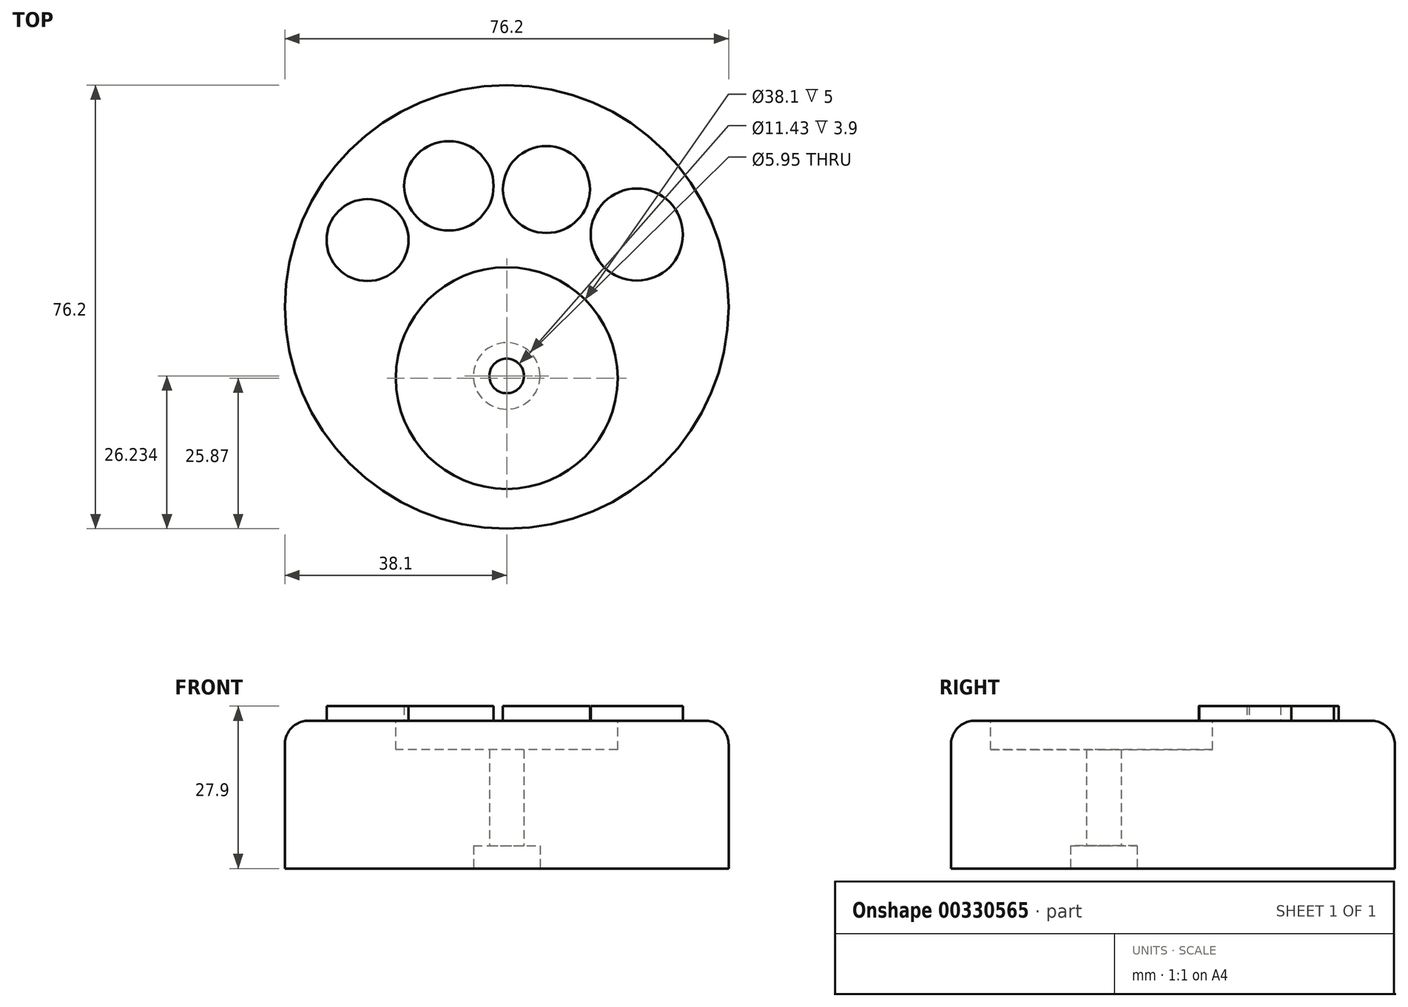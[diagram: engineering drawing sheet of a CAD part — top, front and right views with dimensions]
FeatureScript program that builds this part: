
annotation { "Feature Type Name" : "Feature", "Feature Type Description" : "" }
export const myFeature = defineFeature(function(context is Context, id is Id, definition is map)
    precondition{}
    {
        {
            var Q0;
            Q0=qCreatedBy(makeId("Top.planeOp"),FACE);
            var sketch = newSketch(context, id + "F0", { "sketchPlane" : qUnion([Q0])});
            skCircle(sketch, "E0", {"center": v(0, -4.2) * mm, "radius": 38.1 * mm});
            skSolve(sketch);
        }
        {
            var Q0;
            Q0=qCreatedBy(makeId("Top.planeOp"),FACE);
            var sketch = newSketch(context, id + "F1", { "sketchPlane" : qUnion([Q0])});
            skSolve(sketch);
        }
        {
            var Q0;
            Q0=makeQuery(id+"F1.imprint","IMPRINT",FACE,{"disambiguationData":[TD([[makeQuery(id+"F1.imprint","IMPRINT",EDGE,{"derivedFrom":sQuery(id+"F1.wireOp",EDGE,"EjYEmMLQ-RMnw-RSJ6-Yy3C-PBuiI4cfQdJM.bottom")}),-1.0]])]});
            var Q1;
            Q1=makeQuery(id+"F0.imprint","IMPRINT",FACE,{"disambiguationData":[TD([[makeQuery(id+"F0.imprint","IMPRINT",EDGE,{"derivedFrom":sQuery(id+"F0.wireOp",EDGE,"E0")}),1.0]])]});
            extrude(context, id + "F2", {"entities" : qUnion([Q0, Q1]), "depth" : 25.4 * mm});
        }
        {
            var Q0;
            Q0=makeQuery(id+"F2.opExtrude","CAP_EDGE",EDGE,{"disambiguationData":[OSD([sQuery(id+"F0.wireOp",EDGE,"E0")])],"isStart":false});
            var Q1;
            Q1=makeQuery(id+"F2.opExtrude","CAP_EDGE",EDGE,{"disambiguationData":[OSD([sQuery(id+"F1.wireOp",EDGE,"EjYEmMLQ-RMnw-RSJ6-Yy3C-PBuiI4cfQdJM.left")])],"isStart":false});
            var Q2;
            Q2=makeQuery(id+"F2.opExtrude","CAP_EDGE",EDGE,{"disambiguationData":[OSD([sQuery(id+"F1.wireOp",EDGE,"EjYEmMLQ-RMnw-RSJ6-Yy3C-PBuiI4cfQdJM.top")])],"isStart":false});
            var Q3;
            Q3=makeQuery(id+"F2.opExtrude","CAP_EDGE",EDGE,{"disambiguationData":[OSD([sQuery(id+"F1.wireOp",EDGE,"EjYEmMLQ-RMnw-RSJ6-Yy3C-PBuiI4cfQdJM.right")])],"isStart":false});
            fillet(context, id + "F3", {"entities" : qUnion([Q0, Q1, Q2, Q3]), "radius" : 4.1 * mm, "tangentPropagation" : true, "allowEdgeOverflow" : false});
        }
        {
            var Q0;
            Q0=makeQuery(id+"F2.opExtrude","CAP_FACE",FACE,{"disambiguationData":[OSD([sQuery(id+"F0.wireOp",EDGE,"E0")])],"isStart":false});
            var sketch = newSketch(context, id + "F4", { "sketchPlane" : qUnion([Q0])});
            skCircle(sketch, "E1", {"center": v(0, -17.84) * mm, "radius": 19.05 * mm});
            skCircle(sketch, "E2", {"center": v(22.34, 8.22) * mm, "radius": 7.91 * mm});
            skCircle(sketch, "E3", {"center": v(6.83, 15.98) * mm, "radius": 7.47 * mm});
            skCircle(sketch, "E4", {"center": v(-9.93, 16.6) * mm, "radius": 7.68 * mm});
            skCircle(sketch, "E5", {"center": v(-23.9, 7.3) * mm, "radius": 7.03 * mm});
            skSolve(sketch);
        }
        {
            var Q0;
            Q0=makeQuery(id+"F2.opExtrude","CAP_FACE",FACE,{"disambiguationData":[OSD([sQuery(id+"F0.wireOp",EDGE,"E0")])],"isStart":false});
            var sketch = newSketch(context, id + "F5", { "sketchPlane" : qUnion([Q0])});
            skSolve(sketch);
        }
        {
            var Q0;
            Q0=makeQuery(id+"F4.imprint","IMPRINT",FACE,{"disambiguationData":[TD([[makeQuery(id+"F4.imprint","IMPRINT",EDGE,{"derivedFrom":sQuery(id+"F4.wireOp",EDGE,"E4")}),1.0]])]});
            var Q1;
            Q1=makeQuery(id+"F4.imprint","IMPRINT",FACE,{"disambiguationData":[TD([[makeQuery(id+"F4.imprint","IMPRINT",EDGE,{"derivedFrom":sQuery(id+"F4.wireOp",EDGE,"E3")}),1.0]])]});
            var Q2;
            Q2=makeQuery(id+"F4.imprint","IMPRINT",FACE,{"disambiguationData":[TD([[makeQuery(id+"F4.imprint","IMPRINT",EDGE,{"derivedFrom":sQuery(id+"F4.wireOp",EDGE,"E2")}),1.0]])]});
            var Q3;
            Q3=makeQuery(id+"F4.imprint","IMPRINT",FACE,{"disambiguationData":[TD([[makeQuery(id+"F4.imprint","IMPRINT",EDGE,{"derivedFrom":sQuery(id+"F4.wireOp",EDGE,"E5")}),1.0]])]});
            extrude(context, id + "F6", {"entities" : qUnion([Q0, Q1, Q2, Q3]), "operationType" : NewBodyOperationType.ADD, "depth" : 2.5 * mm});
        }
        {
            var Q0;
            {var subQ0=sQuery(id+"F0.wireOp",EDGE,"E0");Q0=makeQuery(id+"F5.imprint","IMPRINT",FACE,{"disambiguationData":[TD([[makeQuery(id+"F5.imprint","IMPRINT",EDGE,{"derivedFrom":makeQuery(id+"F3.opFillet","BLEND_EDGE",EDGE,{"blendedFrom":[makeQuery(id+"F2.opExtrude","CAP_EDGE",EDGE,{"disambiguationData":[OSD([subQ0])],"isStart":false}),makeQuery(id+"F2.opExtrude","CAP_FACE",FACE,{"disambiguationData":[OSD([subQ0])],"isStart":false})],"blendedInto":[makeQuery(id+"F2.opExtrude","CAP_FACE",FACE,{"disambiguationData":[OSD([subQ0])],"isStart":false})]})}),1.0]])]});}
            var sketch = newSketch(context, id + "F7", { "sketchPlane" : qUnion([Q0])});
            skCircle(sketch, "E6", {"center": v(0, -16.42) * mm, "radius": 19.05 * mm});
            skSolve(sketch);
        }
        {
            var Q0;
            Q0=makeQuery(id+"F7.imprint","IMPRINT",FACE,{"disambiguationData":[TD([[makeQuery(id+"F7.imprint","IMPRINT",EDGE,{"derivedFrom":sQuery(id+"F7.wireOp",EDGE,"E6")}),1.0]])]});
            extrude(context, id + "F8", {"entities" : qUnion([Q0]), "operationType" : NewBodyOperationType.REMOVE, "oppositeDirection" : true, "depth" : 5 * mm});
        }
        {
            var Q0;
            Q0=makeQuery(id+"F2.opExtrude","CAP_FACE",FACE,{"disambiguationData":[OSD([sQuery(id+"F0.wireOp",EDGE,"E0")])],"isStart":true});
            var sketch = newSketch(context, id + "F9", { "sketchPlane" : qUnion([Q0])});
            skCircle(sketch, "E7", {"center": v(0, 16.06) * mm, "radius": 5.72 * mm});
            skSolve(sketch);
        }
        {
            var Q0;
            Q0=makeQuery(id+"F9.imprint","IMPRINT",FACE,{"disambiguationData":[TD([[makeQuery(id+"F9.imprint","IMPRINT",EDGE,{"derivedFrom":sQuery(id+"F9.wireOp",EDGE,"E7")}),1.0]])]});
            extrude(context, id + "F10", {"entities" : qUnion([Q0]), "operationType" : NewBodyOperationType.REMOVE, "oppositeDirection" : true, "depth" : 3.9 * mm});
        }
        {
            var Q0;
            Q0=makeQuery(id+"F10.boolean.opBoolean","COPY",FACE,{"derivedFrom":makeQuery(id+"F10.opExtrude","CAP_FACE",FACE,{"disambiguationData":[OSD([sQuery(id+"F9.wireOp",EDGE,"E7")])],"isStart":false})});
            var sketch = newSketch(context, id + "F11", { "sketchPlane" : qUnion([Q0])});
            skCircle(sketch, "E8", {"center": v(0, 16.06) * mm, "radius": 2.98 * mm});
            skSolve(sketch);
        }
        {
            var Q0;
            Q0=makeQuery(id+"F11.imprint","IMPRINT",FACE,{"disambiguationData":[TD([[makeQuery(id+"F11.imprint","IMPRINT",EDGE,{"derivedFrom":sQuery(id+"F11.wireOp",EDGE,"E8")}),1.0]])]});
            extrude(context, id + "F12", {"entities" : qUnion([Q0]), "operationType" : NewBodyOperationType.REMOVE, "endBound" : BoundingType.THROUGH_ALL, "oppositeDirection" : true, "depth" : 25 * mm});
        }
    });
